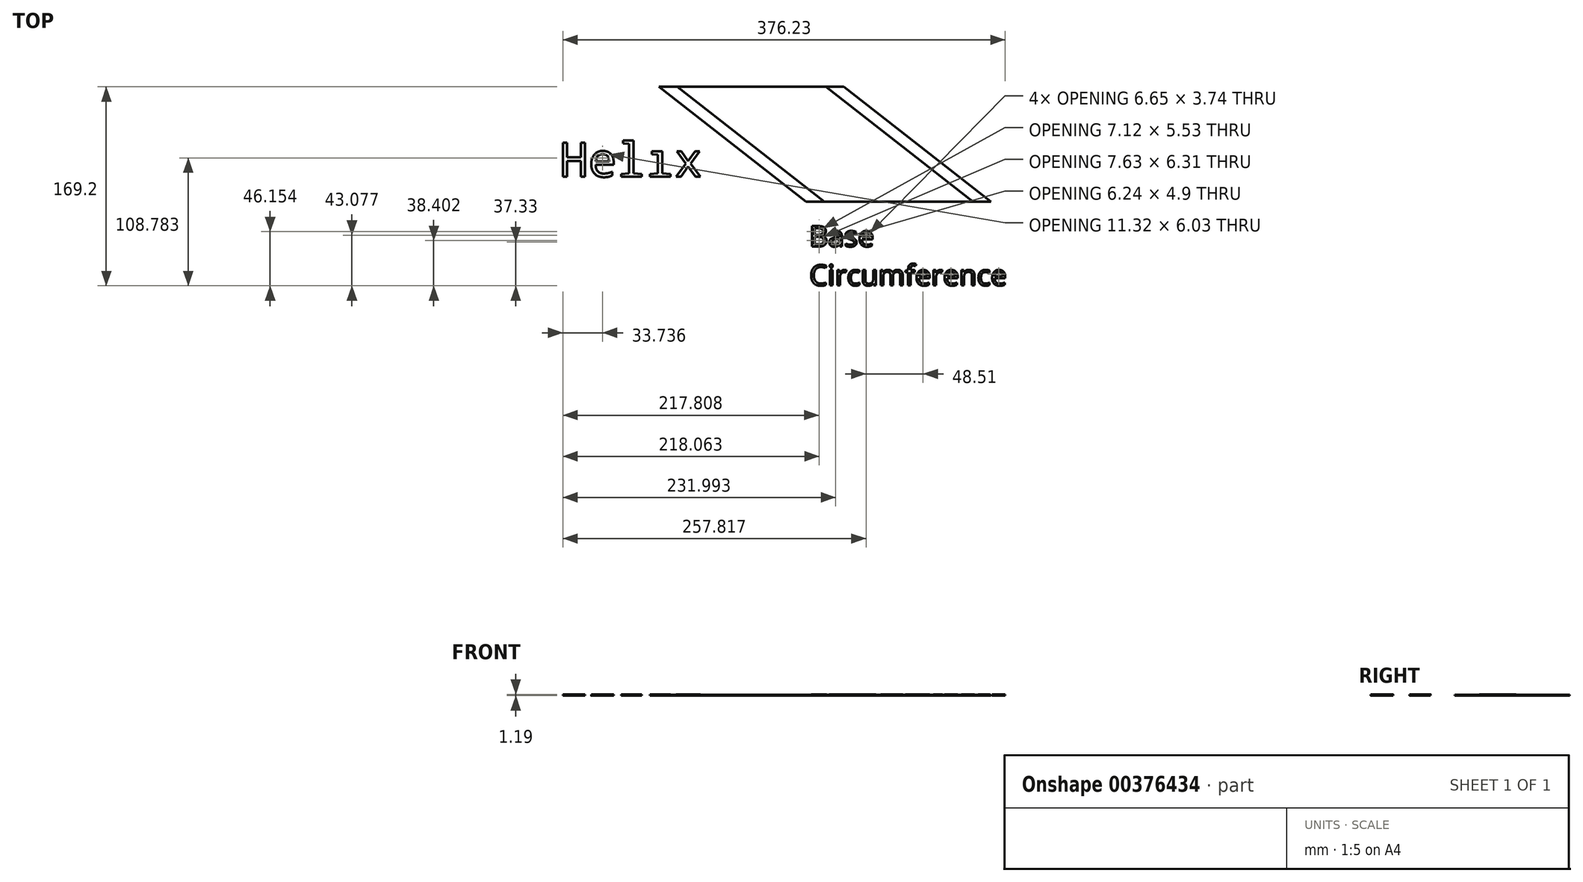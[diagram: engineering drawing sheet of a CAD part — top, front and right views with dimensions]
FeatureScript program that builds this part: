
annotation { "Feature Type Name" : "Feature", "Feature Type Description" : "" }
export const myFeature = defineFeature(function(context is Context, id is Id, definition is map)
    precondition{}
    {
        {
            var Q0;
            Q0=qCreatedBy(makeId("Top.planeOp"),FACE);
            var sketch = newSketch(context, id + "F0", { "sketchPlane" : qUnion([Q0])});
            skLineSegment(sketch, "E0", {"start": v(343.34, -178.45) * mm, "end": v(500.5, -178.45) * mm});
            skLineSegment(sketch, "E1", {"start": v(500.5, -178.45) * mm, "end": v(375.4, -80.72) * mm});
            skLineSegment(sketch, "E2", {"start": v(375.4, -80.72) * mm, "end": v(218.25, -80.72) * mm});
            skLineSegment(sketch, "E3", {"start": v(218.25, -80.72) * mm, "end": v(343.34, -178.45) * mm});
            skLineSegment(sketch, "E4", {"start": v(437.96, -129.59) * mm, "end": v(432.1, -137.1) * mm, "construction": true});
            skLineSegment(sketch, "E5", {"start": v(280.8, -129.59) * mm, "end": v(286.66, -122.08) * mm, "construction": true});
            skLineSegment(sketch, "E6", {"start": v(233.72, -80.72) * mm, "end": v(358.81, -178.45) * mm});
            skLineSegment(sketch, "E7", {"start": v(359.94, -80.72) * mm, "end": v(485.03, -178.45) * mm});
            skText(sketch, "E8", { "text": "Base\nCircumference", "fontName": "NotoSans-Regular.ttf"});
            skLineSegment(sketch, "E9", {"start": v(133.69, -128.1) * mm, "end": v(312, -169.48) * mm, "construction": true});
            skText(sketch, "E10", { "text": "Helix", "fontName": "DroidSansMono.ttf"});
            const initialGuessF0  = {"E8": [0.34605, -0.21653, 1, 0, 0.01755], "E10": [0.13369, -0.15724, 1, 0, 0.02915]};
            skSetInitialGuess(sketch, initialGuessF0);
            skSolve(sketch);
        }
        {
            var Q0;
            {var subQ0=sQuery(id+"F0.wireOp",EDGE,"E6");Q0=makeQuery(id+"F0.imprint","IMPRINT",FACE,{"disambiguationData":[TD([[makeQuery(id+"F0.imprint","IMPRINT",EDGE,{"derivedFrom":subQ0}),1.0]])]});}
            extrude(context, id + "F1", {"entities" : qUnion([Q0]), "depth" : 0.4 * mm});
        }
        {
            var Q0;
            Q0=makeQuery(id+"F0.imprint","IMPRINT",FACE,{"disambiguationData":[TD([[makeQuery(id+"F0.imprint","IMPRINT",EDGE,{"derivedFrom":sQuery(id+"F0.wireOp",EDGE,"E10.sketch_text.stroke-0")}),-1.0]])]});
            var Q1;
            Q1=makeQuery(id+"F0.imprint","IMPRINT",FACE,{"disambiguationData":[TD([[makeQuery(id+"F0.imprint","IMPRINT",EDGE,{"derivedFrom":sQuery(id+"F0.wireOp",EDGE,"E10.sketch_text.stroke-12")}),-1.0]])]});
            var Q2;
            Q2=makeQuery(id+"F0.imprint","IMPRINT",FACE,{"disambiguationData":[TD([[makeQuery(id+"F0.imprint","IMPRINT",EDGE,{"derivedFrom":sQuery(id+"F0.wireOp",EDGE,"E10.sketch_text.stroke-42")}),-1.0]])]});
            var Q3;
            Q3=makeQuery(id+"F0.imprint","IMPRINT",FACE,{"disambiguationData":[TD([[makeQuery(id+"F0.imprint","IMPRINT",EDGE,{"derivedFrom":sQuery(id+"F0.wireOp",EDGE,"E10.sketch_text.stroke-52")}),-1.0]])]});
            var Q4;
            Q4=makeQuery(id+"F0.imprint","IMPRINT",FACE,{"disambiguationData":[TD([[makeQuery(id+"F0.imprint","IMPRINT",EDGE,{"derivedFrom":sQuery(id+"F0.wireOp",EDGE,"E10.sketch_text.stroke-27")}),-1.0]])]});
            var Q5;
            Q5=makeQuery(id+"F0.imprint","IMPRINT",FACE,{"disambiguationData":[TD([[makeQuery(id+"F0.imprint","IMPRINT",EDGE,{"derivedFrom":sQuery(id+"F0.wireOp",EDGE,"E8.sketch_text.stroke-0")}),-1.0]])]});
            var Q6;
            Q6=makeQuery(id+"F0.imprint","IMPRINT",FACE,{"disambiguationData":[TD([[makeQuery(id+"F0.imprint","IMPRINT",EDGE,{"derivedFrom":sQuery(id+"F0.wireOp",EDGE,"E8.sketch_text.stroke-26")}),-1.0]])]});
            var Q7;
            Q7=makeQuery(id+"F0.imprint","IMPRINT",FACE,{"disambiguationData":[TD([[makeQuery(id+"F0.imprint","IMPRINT",EDGE,{"derivedFrom":sQuery(id+"F0.wireOp",EDGE,"E8.sketch_text.stroke-78")}),-1.0]])]});
            var Q8;
            Q8=makeQuery(id+"F0.imprint","IMPRINT",FACE,{"disambiguationData":[TD([[makeQuery(id+"F0.imprint","IMPRINT",EDGE,{"derivedFrom":sQuery(id+"F0.wireOp",EDGE,"E8.sketch_text.stroke-54")}),-1.0]])]});
            var Q9;
            Q9=makeQuery(id+"F0.imprint","IMPRINT",FACE,{"disambiguationData":[TD([[makeQuery(id+"F0.imprint","IMPRINT",EDGE,{"derivedFrom":sQuery(id+"F0.wireOp",EDGE,"E8.sketch_text.stroke-303")}),-1.0]])]});
            var Q10;
            Q10=makeQuery(id+"F0.imprint","IMPRINT",FACE,{"disambiguationData":[TD([[makeQuery(id+"F0.imprint","IMPRINT",EDGE,{"derivedFrom":sQuery(id+"F0.wireOp",EDGE,"E8.sketch_text.stroke-288")}),-1.0]])]});
            var Q11;
            Q11=makeQuery(id+"F0.imprint","IMPRINT",FACE,{"disambiguationData":[TD([[makeQuery(id+"F0.imprint","IMPRINT",EDGE,{"derivedFrom":sQuery(id+"F0.wireOp",EDGE,"E8.sketch_text.stroke-271")}),-1.0]])]});
            var Q12;
            Q12=makeQuery(id+"F0.imprint","IMPRINT",FACE,{"disambiguationData":[TD([[makeQuery(id+"F0.imprint","IMPRINT",EDGE,{"derivedFrom":sQuery(id+"F0.wireOp",EDGE,"E8.sketch_text.stroke-251")}),-1.0]])]});
            var Q13;
            Q13=makeQuery(id+"F0.imprint","IMPRINT",FACE,{"disambiguationData":[TD([[makeQuery(id+"F0.imprint","IMPRINT",EDGE,{"derivedFrom":sQuery(id+"F0.wireOp",EDGE,"E8.sketch_text.stroke-217")}),-1.0]])]});
            var Q14;
            Q14=makeQuery(id+"F0.imprint","IMPRINT",FACE,{"disambiguationData":[TD([[makeQuery(id+"F0.imprint","IMPRINT",EDGE,{"derivedFrom":sQuery(id+"F0.wireOp",EDGE,"E8.sketch_text.stroke-237")}),-1.0]])]});
            var Q15;
            Q15=makeQuery(id+"F0.imprint","IMPRINT",FACE,{"disambiguationData":[TD([[makeQuery(id+"F0.imprint","IMPRINT",EDGE,{"derivedFrom":sQuery(id+"F0.wireOp",EDGE,"E8.sketch_text.stroke-199")}),-1.0]])]});
            var Q16;
            Q16=makeQuery(id+"F0.imprint","IMPRINT",FACE,{"disambiguationData":[TD([[makeQuery(id+"F0.imprint","IMPRINT",EDGE,{"derivedFrom":sQuery(id+"F0.wireOp",EDGE,"E8.sketch_text.stroke-172")}),-1.0]])]});
            var Q17;
            Q17=makeQuery(id+"F0.imprint","IMPRINT",FACE,{"disambiguationData":[TD([[makeQuery(id+"F0.imprint","IMPRINT",EDGE,{"derivedFrom":sQuery(id+"F0.wireOp",EDGE,"E8.sketch_text.stroke-155")}),-1.0]])]});
            var Q18;
            Q18=makeQuery(id+"F0.imprint","IMPRINT",FACE,{"disambiguationData":[TD([[makeQuery(id+"F0.imprint","IMPRINT",EDGE,{"derivedFrom":sQuery(id+"F0.wireOp",EDGE,"E8.sketch_text.stroke-140")}),-1.0]])]});
            var Q19;
            Q19=makeQuery(id+"F0.imprint","IMPRINT",FACE,{"disambiguationData":[TD([[makeQuery(id+"F0.imprint","IMPRINT",EDGE,{"derivedFrom":sQuery(id+"F0.wireOp",EDGE,"E8.sketch_text.stroke-126")}),-1.0]])]});
            var Q20;
            Q20=makeQuery(id+"F0.imprint","IMPRINT",FACE,{"disambiguationData":[TD([[makeQuery(id+"F0.imprint","IMPRINT",EDGE,{"derivedFrom":sQuery(id+"F0.wireOp",EDGE,"E8.sketch_text.stroke-114")}),-1.0]])]});
            var Q21;
            Q21=makeQuery(id+"F0.imprint","IMPRINT",FACE,{"disambiguationData":[TD([[makeQuery(id+"F0.imprint","IMPRINT",EDGE,{"derivedFrom":sQuery(id+"F0.wireOp",EDGE,"E8.sketch_text.stroke-118")}),-1.0]])]});
            var Q22;
            Q22=makeQuery(id+"F0.imprint","IMPRINT",FACE,{"disambiguationData":[TD([[makeQuery(id+"F0.imprint","IMPRINT",EDGE,{"derivedFrom":sQuery(id+"F0.wireOp",EDGE,"E8.sketch_text.stroke-98")}),-1.0]])]});
            extrude(context, id + "F2", {"entities" : qUnion([Q0, Q1, Q2, Q3, Q4, Q5, Q6, Q7, Q8, Q9, Q10, Q11, Q12, Q13, Q14, Q15, Q16, Q17, Q18, Q19, Q20, Q21, Q22]), "depth" : 1.2 * mm});
        }
        {
            var Q0;
            {var subQ0=sQuery(id+"F0.wireOp",EDGE,"E3");Q0=makeQuery(id+"F0.imprint","IMPRINT",FACE,{"disambiguationData":[TD([[makeQuery(id+"F0.imprint","IMPRINT",EDGE,{"derivedFrom":subQ0}),1.0]])]});}
            var Q1;
            {var subQ0=sQuery(id+"F0.wireOp",EDGE,"E1");Q1=makeQuery(id+"F0.imprint","IMPRINT",FACE,{"disambiguationData":[TD([[makeQuery(id+"F0.imprint","IMPRINT",EDGE,{"derivedFrom":subQ0}),1.0]])]});}
            extrude(context, id + "F3", {"entities" : qUnion([Q0, Q1]), "operationType" : NewBodyOperationType.ADD, "depth" : 0.8 * mm});
        }
    });
